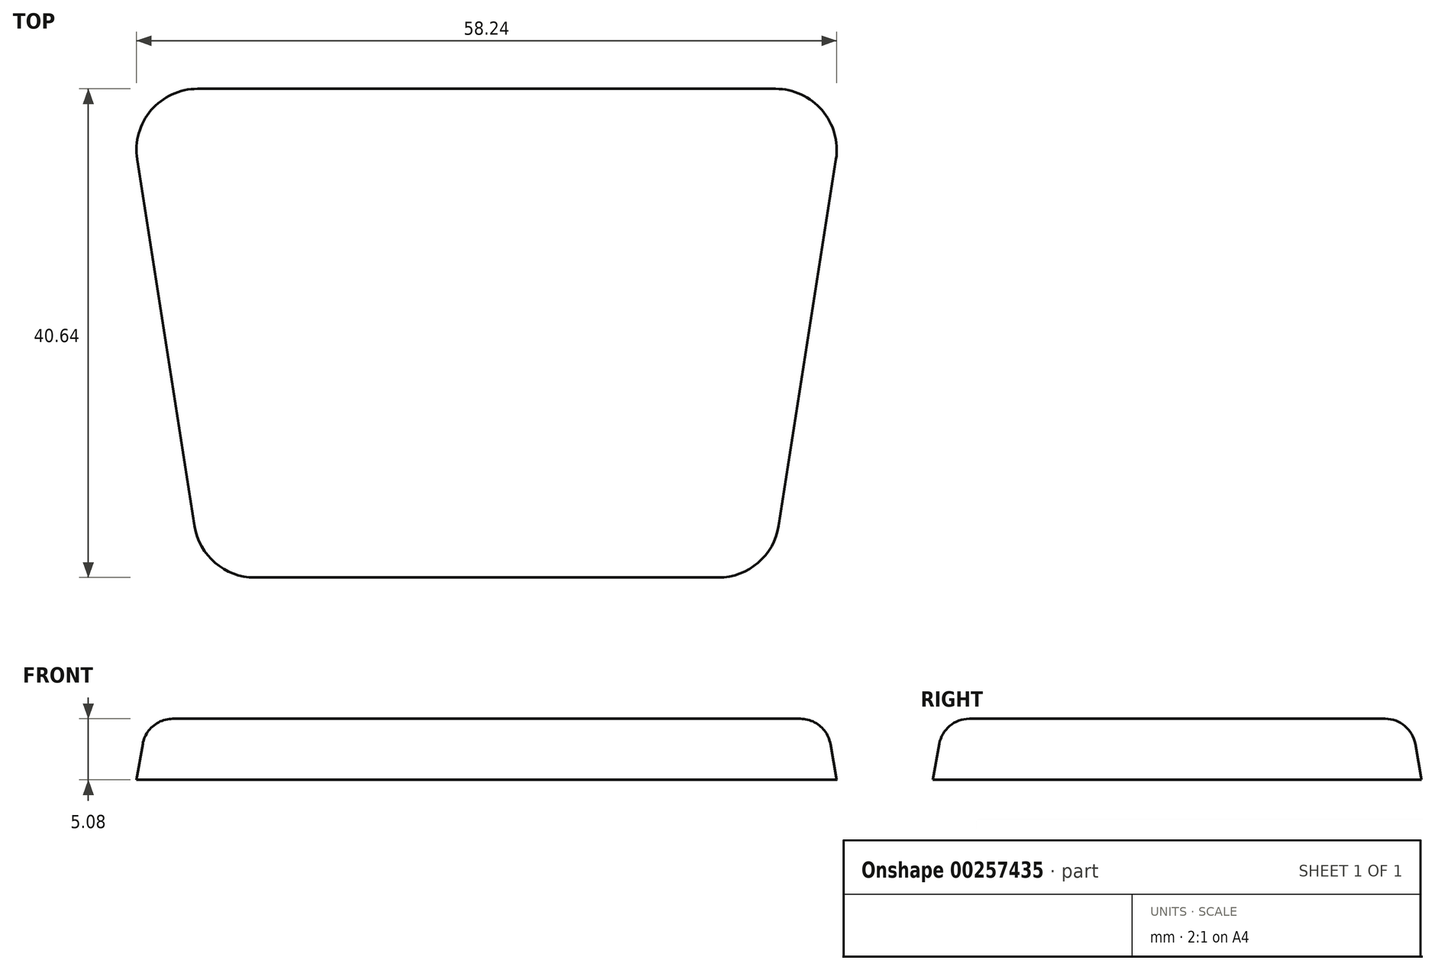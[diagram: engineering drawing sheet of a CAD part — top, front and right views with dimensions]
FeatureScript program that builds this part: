
annotation { "Feature Type Name" : "Feature", "Feature Type Description" : "" }
export const myFeature = defineFeature(function(context is Context, id is Id, definition is map)
    precondition{}
    {
        {
            var Q0;
            Q0=qCreatedBy(makeId("Top.planeOp"),FACE);
            var sketch = newSketch(context, id + "F0", { "sketchPlane" : qUnion([Q0])});
            skLineSegment(sketch, "E0", {"start": v(-17.62, 22.15) * mm, "end": v(-41.66, 22.15) * mm});
            skPoint(sketch, "E0.startSnap0", {"position": v(-17.62, 16.78) * mm});
            skLineSegment(sketch, "E1", {"start": v(-46.68, 16.28) * mm, "end": v(-41.92, -14.2) * mm});
            skLineSegment(sketch, "E2", {"start": v(-36.9, -18.5) * mm, "end": v(-18.74, -18.5) * mm});
            skPoint(sketch, "E3.visualSharp", {"position": v(-47.6, 22.15) * mm});
            skArc(sketch, "E3.filletArc", {"start": v(-41.66, 22.15) * mm, "mid": v(-45.52, 20.37) * mm, "end": v(-46.68, 16.28) * mm});
            skPoint(sketch, "E4.visualSharp", {"position": v(-41.25, -18.5) * mm});
            skArc(sketch, "E4.filletArc", {"start": v(-41.92, -14.2) * mm, "mid": v(-40.2, -17.27) * mm, "end": v(-36.9, -18.5) * mm});
            skLineSegment(sketch, "E5.MirrorCS", {"start": v(-17.62, 22.15) * mm, "end": v(6.42, 22.15) * mm});
            skArc(sketch, "E6.MirrorCS", {"start": v(6.42, 22.15) * mm, "mid": v(10.28, 20.37) * mm, "end": v(11.44, 16.28) * mm});
            skLineSegment(sketch, "E7.MirrorCS", {"start": v(11.44, 16.28) * mm, "end": v(6.67, -14.2) * mm});
            skArc(sketch, "E8.MirrorCS", {"start": v(6.67, -14.2) * mm, "mid": v(4.95, -17.27) * mm, "end": v(1.65, -18.5) * mm});
            skLineSegment(sketch, "E9.MirrorCS", {"start": v(1.65, -18.5) * mm, "end": v(-16.5, -18.5) * mm});
            skLineSegment(sketch, "E10", {"start": v(-18.74, -18.5) * mm, "end": v(-16.5, -18.5) * mm});
            skSolve(sketch);
        }
        {
            var Q0;
            Q0 = qSketchRegion(id + "F0", true);
            extrude(context, id + "F1", {"entities" : qUnion([Q0]), "depth" : 5.08 * mm, "hasDraft" : true, "draftAngle" : 10 * degree, "draftPullDirection" : true});
        }
        {
            var Q0;
            Q0=makeQuery(id+"F1.opExtrude","CAP_FACE",FACE,{"disambiguationData":[OSD([sQuery(id+"F0.wireOp",EDGE,"E0"),sQuery(id+"F0.wireOp",EDGE,"E1"),sQuery(id+"F0.wireOp",EDGE,"E2"),sQuery(id+"F0.wireOp",EDGE,"E3.filletArc"),sQuery(id+"F0.wireOp",EDGE,"E4.filletArc"),sQuery(id+"F0.wireOp",EDGE,"E5.MirrorCS"),sQuery(id+"F0.wireOp",EDGE,"E6.MirrorCS"),sQuery(id+"F0.wireOp",EDGE,"E7.MirrorCS"),sQuery(id+"F0.wireOp",EDGE,"E8.MirrorCS"),sQuery(id+"F0.wireOp",EDGE,"E9.MirrorCS"),sQuery(id+"F0.wireOp",EDGE,"E10")])],"isStart":false});
            fillet(context, id + "F2", {"entities" : qUnion([Q0]), "radius" : 2.54 * mm, "tangentPropagation" : true, "allowEdgeOverflow" : false});
        }
    });
